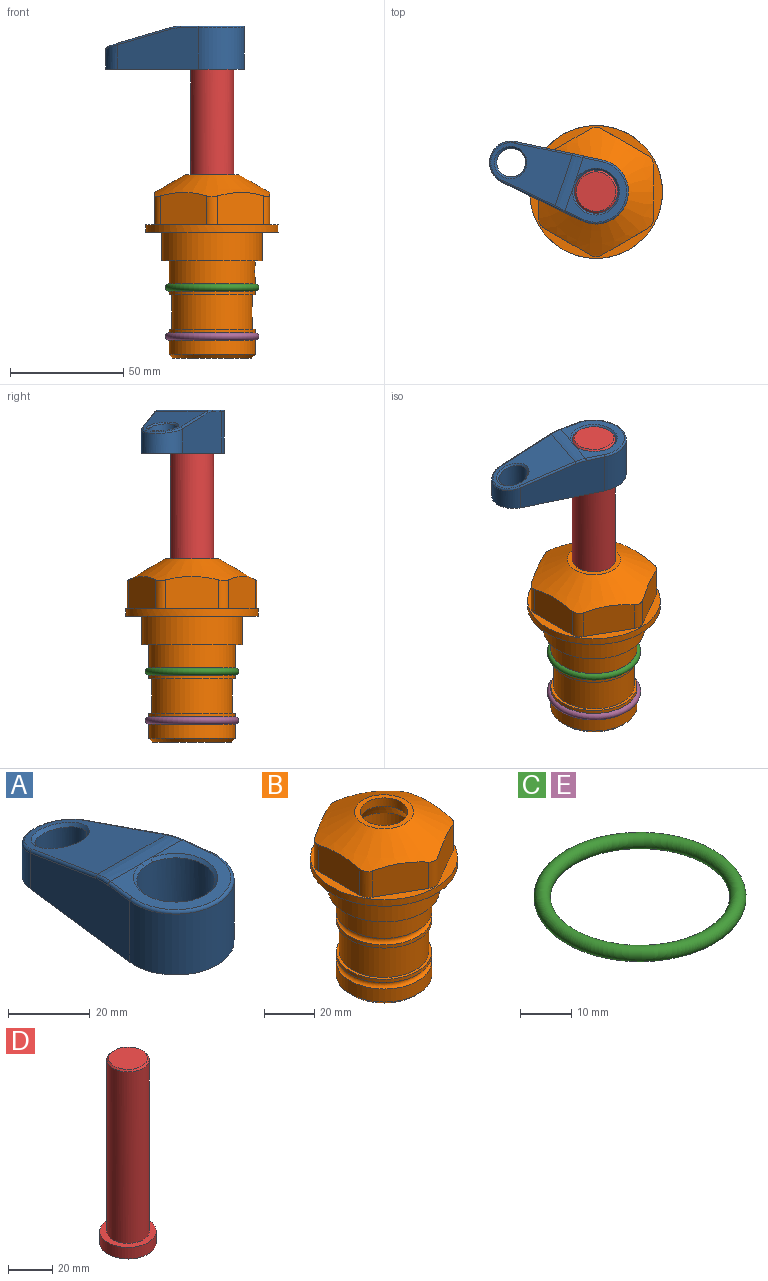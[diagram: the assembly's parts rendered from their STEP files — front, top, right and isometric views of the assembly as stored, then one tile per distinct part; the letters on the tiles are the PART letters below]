
ASSEMBLY  parts=5 mates=4
PART A: 31 faces, bbox 31.7x65.5x19.8 mm
  f0: plane 39.12x18.26mm, normal (0.99,0.12,0), area 612.2mm2, adj f1,f4,f7,f11,f13,f15
  f1: cylinder r=9.53mm len=18.91mm, axis (0,0,-1), area 296.1mm2, adj f0,f2,f7,f17
  f2: plane 39.12x18.26mm, normal (-0.99,0.12,0), area 612.2mm2, adj f1,f4,f7,f12,f14,f16
  f3: cylinder r=6.35mm len=12.7mm, axis (0,0,-1), area 362.4mm2, adj f7,f18
  f4: cylinder r=14.29mm len=28.58mm, axis (0,0,-1), area 882.2mm2, adj f0,f2,f7,f10
  f5: cylinder r=9.53mm len=19.05mm, axis (0,0,-1), area 1092.6mm2, adj f7,f19,f20
  f6: plane 26.99x23.69mm, normal (0,0,1), area 216.2mm2, adj f9,f10,f11,f12,f19
  f7: plane 63.5x28.58mm, normal (0,0,-1), area 661.8mm2, adj f0,f1,f2,f3,f4,f5,f22,f23
  f8: plane 33.52x23.6mm, normal (0,0.26,0.97), area 486mm2, adj f9,f15,f16,f17,f18
  f9: cylinder r=19.05mm len=24.72mm, axis (1,0,0), area 120.4mm2, adj f6,f8,f13,f14,f20
  f10: torus R=13.49mm, axis (0,0,1), area 59mm2, adj f4,f6,f11,f12
  f11: cylinder r=0.79mm len=8.67mm, axis (0.12,-0.99,0), area 10.8mm2, adj f0,f6,f10,f13
  f12: cylinder r=0.79mm len=8.67mm, axis (0.12,0.99,0), area 10.8mm2, adj f2,f6,f10,f14
  f13: bspline ~4.95x1.42mm, area 6.1mm2, adj f0,f9,f11,f15
  f14: bspline ~4.95x1.42mm, area 6.1mm2, adj f2,f9,f12,f16
  f15: cylinder r=0.79mm len=25.95mm, axis (0.12,-0.96,0.26), area 32.9mm2, adj f0,f8,f13,f17
  f16: cylinder r=0.79mm len=25.95mm, axis (0.12,0.96,-0.26), area 32.9mm2, adj f2,f8,f14,f17
  f17: bspline ~18.91x8.38mm, area 30mm2, adj f1,f8,f15,f16
  f18: bspline ~14.29x14.29mm, area 48.3mm2, adj f3,f8
  f19: cone r=9.53mm half-angle=45deg, axis (0,0,1), area 66.5mm2, adj f5,f6,f20
  f20: bspline ~3.22x0.96mm, area 3.5mm2, adj f5,f9,f19
  f21: plane 2.75x2.72mm, normal (0,0,-1), area 2.9mm2, adj f23,f25,f28
  f22: plane 23.05x15.88mm, normal (-0.99,-0.12,0), area 323.6mm2, adj f7,f25,f26,f27,f28,f29
  f23: plane 23.05x15.88mm, normal (0.99,-0.12,0), area 323.6mm2, adj f7,f21,f25,f27,f28,f30
  f24: cylinder r=9.53mm len=10.69mm, axis (0,0,-1), area 114.7mm2, adj f7,f27,f29,f30
  f25: cylinder r=12.7mm len=20.59mm, axis (0,0,-1), area 381.1mm2, adj f7,f21,f22,f23,f26,f28
  f26: plane 2.75x2.72mm, normal (0,0,-1), area 2.9mm2, adj f22,f25,f28
  f27: plane 19.72x18.37mm, normal (0,-0.26,-0.97), area 291.8mm2, adj f22,f23,f24,f28,f29,f30
  f28: cylinder r=15.88mm len=19.92mm, axis (1,0,0), area 54.8mm2, adj f21,f22,f23,f25,f26,f27
  f29: cylinder r=1.59mm len=11mm, axis (0,0,-1), area 34.7mm2, adj f7,f22,f24,f27
  f30: cylinder r=1.59mm len=11mm, axis (0,0,-1), area 34.7mm2, adj f7,f23,f24,f27
PART B: 36 faces, bbox 58.7x58.7x81 mm
  f0: cylinder r=17.78mm len=35.56mm, axis (0,0,1), area 1670.8mm2, adj f23,f24,f31
  f1: cylinder r=19.05mm len=38.1mm, axis (0,0,1), area 1191.9mm2, adj f26,f27,f30
  f2: plane 58.66x58.66mm, normal (0,0,-1), area 1150.6mm2, adj f3,f28
  f3: cylinder r=29.33mm len=58.66mm, axis (0,0,-1), area 585.1mm2, adj f2,f4
  f4: plane 58.66x58.66mm, normal (0,0,1), area 475.9mm2, adj f3,f5,f6,f7,f8,f9,f10,f11
  f5: plane 20.32x14.34mm, normal (-0.5,0.87,0), area 324.4mm2, adj f4,f15,f16,f17
  f6: plane 20.32x14.34mm, normal (0.5,0.87,0), area 324.4mm2, adj f4,f14,f15,f17
  f7: plane 23.48x14.34mm, normal (1,0,0), area 324.4mm2, adj f4,f13,f14,f17
  f8: plane 20.32x14.34mm, normal (0.5,-0.87,0), area 324.4mm2, adj f4,f12,f13,f17
  f9: plane 20.32x14.34mm, normal (-0.5,-0.87,0), area 324.4mm2, adj f4,f11,f12,f17
  f10: plane 23.48x14.34mm, normal (-1,0,0), area 324.4mm2, adj f4,f11,f16,f17
  f11: cylinder r=5.08mm len=12.85mm, axis (0,0,-1), area 67.2mm2, adj f4,f9,f10,f17
  f12: cylinder r=5.08mm len=12.85mm, axis (0,0,-1), area 67.2mm2, adj f4,f8,f9,f17
  f13: cylinder r=5.08mm len=12.85mm, axis (0,0,-1), area 67.2mm2, adj f4,f7,f8,f17
  f14: cylinder r=5.08mm len=12.85mm, axis (0,0,-1), area 67.2mm2, adj f4,f6,f7,f17
  f15: cylinder r=5.08mm len=12.85mm, axis (0,0,-1), area 67.2mm2, adj f4,f5,f6,f17
  f16: cylinder r=5.08mm len=12.85mm, axis (0,0,-1), area 67.2mm2, adj f4,f5,f10,f17
  f17: cone r=11.73mm half-angle=60deg, axis (0,0,-1), area 2071.8mm2, adj f5,f6,f7,f8,f9,f10,f11,f12
  f18: plane 23.46x23.46mm, normal (0,0,1), area 147.4mm2, adj f17,f35
  f19: plane 34.93x34.93mm, normal (0,0,-1), area 958mm2, adj f29
  f20: cylinder r=19.05mm len=38.1mm, axis (0,0,1), area 760.1mm2, adj f21,f29
  f21: torus R=19.05mm, axis (0,0,1), area 565.3mm2, adj f20,f22
  f22: cylinder r=19.05mm len=38.1mm, axis (0,0,1), area 190mm2, adj f21,f23
  f23: plane 38.1x38.1mm, normal (0,0,1), area 146.9mm2, adj f0,f22
  f24: plane 38.1x38.1mm, normal (0,0,-1), area 146.9mm2, adj f0,f25
  f25: cylinder r=19.05mm len=38.1mm, axis (0,0,1), area 190mm2, adj f24,f26
  f26: torus R=19.05mm, axis (0,0,1), area 565.3mm2, adj f1,f25
  f27: plane 44.45x44.45mm, normal (0,0,-1), area 411.7mm2, adj f1,f28
  f28: cylinder r=22.23mm len=44.45mm, axis (0,0,1), area 1773.5mm2, adj f2,f27
  f29: cone r=19.05mm half-angle=45deg, axis (0,0,1), area 257.5mm2, adj f19,f20
  f30: cylinder r=3.17mm len=6.75mm, axis (-1,0,0), area 128mm2, adj f1,f33
  f31: cylinder r=3.17mm len=6.35mm, axis (-1,0,0), area 102.5mm2, adj f0,f33
  f32: plane 25.4x25.4mm, normal (0,0,1), area 506.7mm2, adj f33
  f33: cylinder r=12.7mm len=66.42mm, axis (0,0,-1), area 5236.2mm2, adj f30,f31,f32,f34
  f34: cone r=9.53mm half-angle=30deg, axis (0,0,-1), area 443.4mm2, adj f33,f35
  f35: cylinder r=9.53mm len=19.05mm, axis (0,0,-1), area 240.9mm2, adj f18,f34
PART C: 1 faces, bbox 44.7x44.7x3.2 mm
  f0: torus R=19.05mm, axis (0,0,1), area 1193.9mm2
PART D: 6 faces, bbox 25.4x25.4x101.6 mm
  f0: plane 17.46x17.46mm, normal (0,0,1), area 239.5mm2, adj f5
  f1: plane 25.4x25.4mm, normal (0,0,-1), area 506.7mm2, adj f2
  f2: cylinder r=12.7mm len=25.4mm, axis (0,0,1), area 506.7mm2, adj f1,f3
  f3: plane 25.4x25.4mm, normal (0,0,1), area 221.7mm2, adj f2,f4
  f4: cylinder r=9.53mm len=94.46mm, axis (0,0,1), area 5653mm2, adj f3,f5
  f5: cone r=8.73mm half-angle=45deg, axis (0,0,-1), area 64.4mm2, adj f0,f4
PART E: same geometry as C
PLACE A rot(axis=(0,0,1),71.1deg) t=(0,0,27.55)mm
PLACE B at identity fixed
PLACE C at identity
PLACE D rot(axis=(0,0,1),71.1deg) t=(0,0,27.55)mm
PLACE E t=(0,0,-21.59)mm
MATE fastened C.f0 <-> B.f0  axis (0,0,1) through (0,0,-24.51)mm
MATE fastened E.f0 <-> B.f0  axis (0,0,1) through (0,0,-46.1)mm
MATE fastened A.f4 <-> D.f2  axis (0,0,1) through (0,0,91.05)mm
MATE cylindrical D.f2 <-> B.f0  axis (0,0,-1) through (0,0,-10.55)mm
